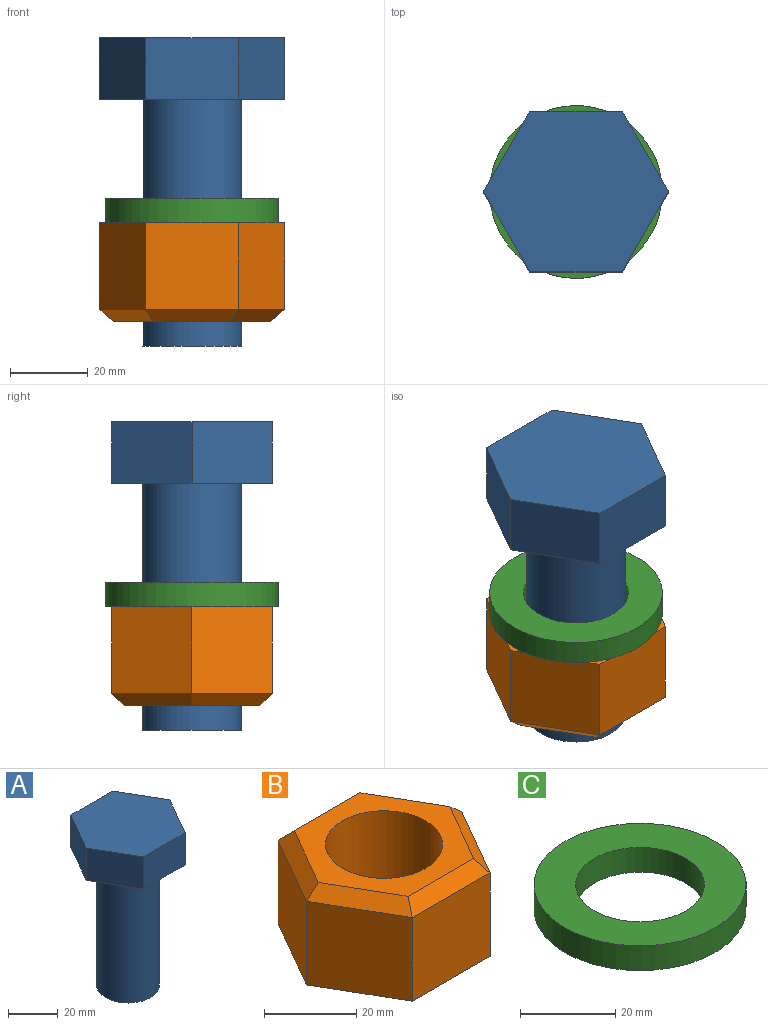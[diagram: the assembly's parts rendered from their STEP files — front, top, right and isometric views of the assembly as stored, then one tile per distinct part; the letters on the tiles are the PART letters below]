
ASSEMBLY  parts=3 mates=2
PART A: 10 faces, bbox 47.7x41.3x79.4 mm
  f0: cylinder r=12.7mm len=63.5mm, axis (0,0,1), area 5067.1mm2, adj f1,f9
  f1: plane 25.4x25.4mm, normal (0,0,-1), area 506.7mm2, adj f0
  f2: plane 20.64x15.88mm, normal (-0.87,0.5,0), area 378.3mm2, adj f3,f7,f8,f9
  f3: plane 20.64x15.88mm, normal (-0.87,-0.5,0), area 378.3mm2, adj f2,f4,f8,f9
  f4: plane 23.83x15.88mm, normal (0,-1,0), area 378.3mm2, adj f3,f5,f8,f9
  f5: plane 20.64x15.88mm, normal (0.87,-0.5,0), area 378.3mm2, adj f4,f6,f8,f9
  f6: plane 20.64x15.88mm, normal (0.87,0.5,0), area 378.3mm2, adj f5,f7,f8,f9
  f7: plane 23.83x15.88mm, normal (0,1,0), area 378.3mm2, adj f2,f6,f8,f9
  f8: plane 47.66x41.28mm, normal (0,0,1), area 1475.4mm2, adj f2,f3,f4,f5,f6,f7
  f9: plane 47.66x41.28mm, normal (0,0,-1), area 968.7mm2, adj f0,f2,f3,f4,f5,f6,f7
PART B: 15 faces, bbox 47.7x41.3x25.4 mm
  f0: plane 22.23x20.64mm, normal (-0.87,0.5,0), area 529.6mm2, adj f1,f6,f8,f9
  f1: plane 22.23x20.64mm, normal (-0.87,-0.5,0), area 529.6mm2, adj f0,f2,f8,f11
  f2: plane 23.83x22.23mm, normal (0,-1,0), area 529.6mm2, adj f1,f3,f8,f13
  f3: plane 22.23x20.64mm, normal (0.87,-0.5,0), area 529.6mm2, adj f2,f4,f8,f14
  f4: plane 22.23x20.64mm, normal (0.87,0.5,0), area 529.6mm2, adj f3,f6,f8,f12
  f5: cylinder r=12.7mm len=25.4mm, axis (0,0,-1), area 2026.8mm2, adj f7,f8
  f6: plane 23.83x22.23mm, normal (0,1,0), area 529.6mm2, adj f0,f4,f8,f10
  f7: plane 40.33x34.93mm, normal (0,0,1), area 549.6mm2, adj f5,f9,f10,f11,f12,f13,f14
  f8: plane 47.66x41.28mm, normal (0,0,-1), area 968.7mm2, adj f0,f1,f2,f3,f4,f5,f6
  f9: plane 20.64x13.75mm, normal (-0.61,0.35,0.71), area 98.8mm2, adj f0,f7,f10,f11
  f10: plane 23.83x3.18mm, normal (0,0.71,0.71), area 98.8mm2, adj f6,f7,f9,f12
  f11: plane 20.64x13.75mm, normal (-0.61,-0.35,0.71), area 98.8mm2, adj f1,f7,f9,f13
  f12: plane 20.64x13.75mm, normal (0.61,0.35,0.71), area 98.8mm2, adj f4,f7,f10,f14
  f13: plane 23.83x3.18mm, normal (0,-0.71,0.71), area 98.8mm2, adj f2,f7,f11,f14
  f14: plane 20.64x13.75mm, normal (0.61,-0.35,0.71), area 98.8mm2, adj f3,f7,f12,f13
PART C: 4 faces, bbox 44.5x44.5x6.4 mm
  f0: cylinder r=13.49mm len=26.99mm, axis (0,0,-1), area 538.4mm2, adj f2,f3
  f1: cylinder r=22.23mm len=44.45mm, axis (0,0,-1), area 886.7mm2, adj f2,f3
  f2: plane 44.45x44.45mm, normal (0,0,1), area 979.8mm2, adj f0,f1
  f3: plane 44.45x44.45mm, normal (0,0,-1), area 979.8mm2, adj f0,f1
PLACE A t=(-27.37,-17.2,21.71)mm
PLACE B rot(axis=(1,0,0),180deg) t=(-27.37,-17.2,-10.04)mm
PLACE C rot(axis=(1,0,0),180deg) t=(-27.37,-17.2,-3.69)mm
MATE fastened C.f0 <-> B.f5  axis (0,0,-1) through (-27.37,-17.2,-10.04)mm
MATE fastened B.f5 <-> A.f0  axis (0,0,-1) through (-27.37,-17.2,-35.44)mm
